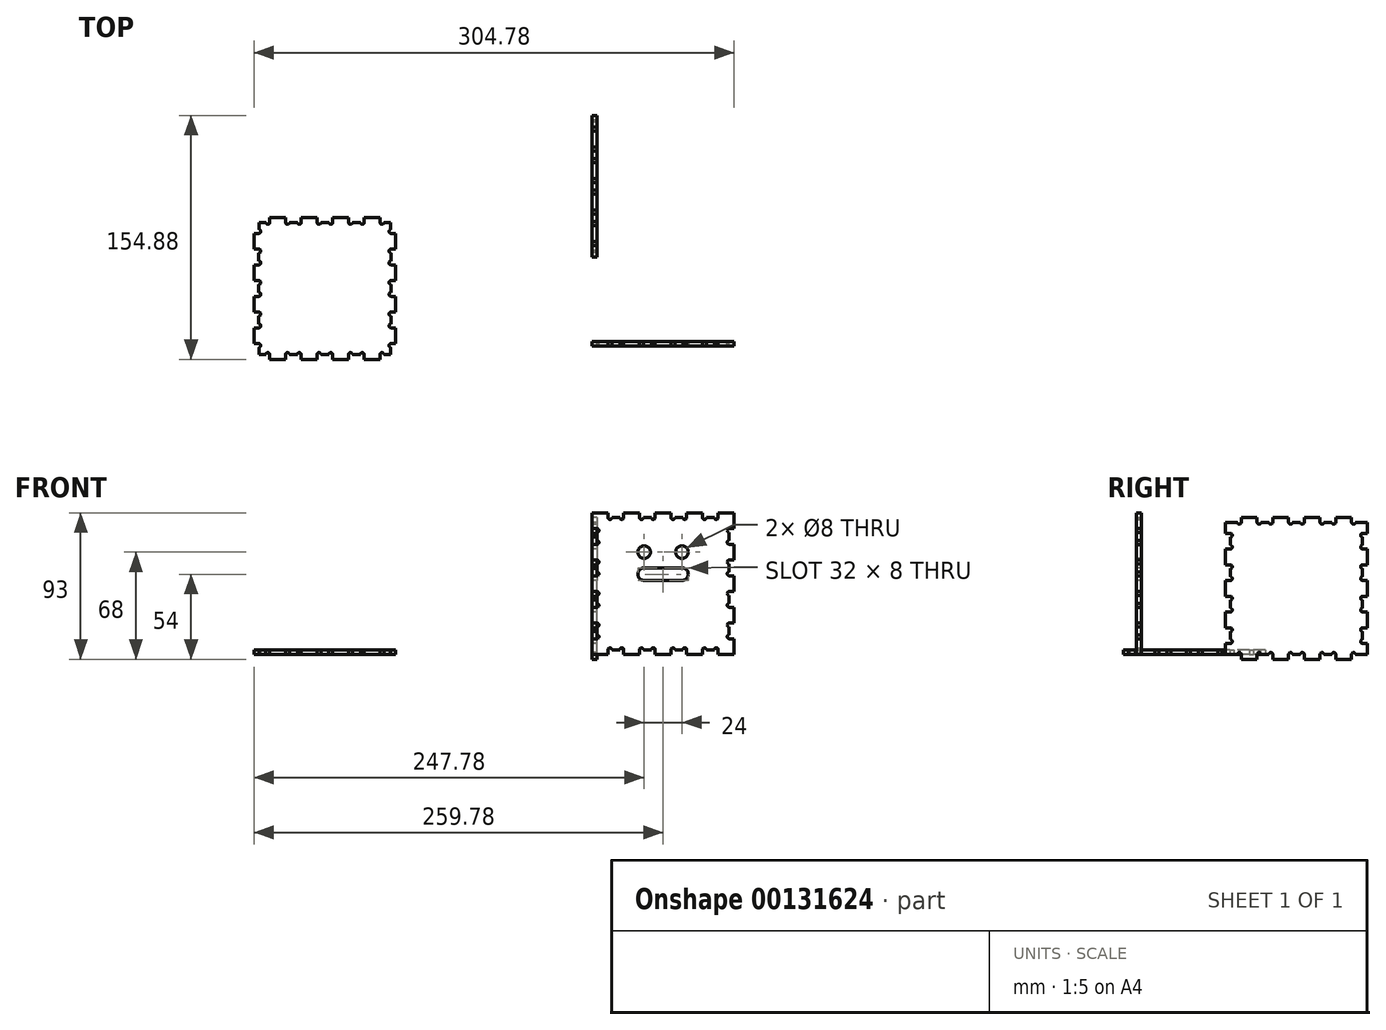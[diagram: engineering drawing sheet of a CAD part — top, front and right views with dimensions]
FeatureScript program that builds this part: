
annotation { "Feature Type Name" : "Feature", "Feature Type Description" : "" }
export const myFeature = defineFeature(function(context is Context, id is Id, definition is map)
    precondition{}
    {
        {
            var Q0;
            Q0=qCreatedBy(makeId("Front.planeOp"),FACE);
            var sketch = newSketch(context, id + "F0", { "sketchPlane" : qUnion([Q0])});
            skLineSegment(sketch, "E0.top", {"start": v(0, 90) * mm, "end": v(10, 90) * mm});
            skLineSegment(sketch, "E0.left", {"start": v(0, 0) * mm, "end": v(0, 10) * mm});
            skLineSegment(sketch, "E1.top", {"start": v(12.5, 87) * mm, "end": v(17.5, 87) * mm});
            skLineSegment(sketch, "E1.left", {"start": v(10, 90) * mm, "end": v(10, 87) * mm});
            skLineSegment(sketch, "E1.right", {"start": v(20, 90) * mm, "end": v(20, 87) * mm});
            skArc(sketch, "E2", {"start": v(10, 87) * mm, "mid": v(11.25, 85.75) * mm, "end": v(12.5, 87) * mm});
            skArc(sketch, "E3", {"start": v(17.5, 87) * mm, "mid": v(18.75, 85.75) * mm, "end": v(20, 87) * mm});
            skLineSegment(sketch, "E4.trimOffspring", {"start": v(20, 90) * mm, "end": v(30, 90) * mm});
            skLineSegment(sketch, "E5.1.0.0", {"start": v(32.5, 87) * mm, "end": v(37.5, 87) * mm});
            skLineSegment(sketch, "E5.1.0.1", {"start": v(30, 90) * mm, "end": v(30, 87) * mm});
            skLineSegment(sketch, "E5.1.0.2", {"start": v(40, 90) * mm, "end": v(40, 87) * mm});
            skArc(sketch, "E5.1.0.3", {"start": v(37.5, 87) * mm, "mid": v(38.75, 85.75) * mm, "end": v(40, 87) * mm});
            skArc(sketch, "E5.1.0.4", {"start": v(30, 87) * mm, "mid": v(31.25, 85.75) * mm, "end": v(32.5, 87) * mm});
            skLineSegment(sketch, "E5.2.0.0", {"start": v(52.5, 87) * mm, "end": v(57.5, 87) * mm});
            skLineSegment(sketch, "E5.2.0.1", {"start": v(50, 90) * mm, "end": v(50, 87) * mm});
            skLineSegment(sketch, "E5.2.0.2", {"start": v(60, 90) * mm, "end": v(60, 87) * mm});
            skArc(sketch, "E5.2.0.3", {"start": v(57.5, 87) * mm, "mid": v(58.75, 85.75) * mm, "end": v(60, 87) * mm});
            skArc(sketch, "E5.2.0.4", {"start": v(50, 87) * mm, "mid": v(51.25, 85.75) * mm, "end": v(52.5, 87) * mm});
            skLineSegment(sketch, "E5.3.0.0", {"start": v(72.5, 87) * mm, "end": v(77.5, 87) * mm});
            skLineSegment(sketch, "E5.3.0.1", {"start": v(70, 90) * mm, "end": v(70, 87) * mm});
            skLineSegment(sketch, "E5.3.0.2", {"start": v(80, 90) * mm, "end": v(80, 87) * mm});
            skArc(sketch, "E5.3.0.3", {"start": v(77.5, 87) * mm, "mid": v(78.75, 85.75) * mm, "end": v(80, 87) * mm});
            skArc(sketch, "E5.3.0.4", {"start": v(70, 87) * mm, "mid": v(71.25, 85.75) * mm, "end": v(72.5, 87) * mm});
            skLineSegment(sketch, "E5.direction1", {"start": v(10, 87) * mm, "end": v(30, 87) * mm, "construction": true});
            skLineSegment(sketch, "E6.trimOffspring", {"start": v(40, 90) * mm, "end": v(50, 90) * mm});
            skLineSegment(sketch, "E7.trimOffspring", {"start": v(60, 90) * mm, "end": v(70, 90) * mm});
            skLineSegment(sketch, "E8", {"start": v(0, 45) * mm, "end": v(0, 45) * mm});
            skLineSegment(sketch, "E9.MirrorCS", {"start": v(10, 3) * mm, "end": v(30, 3) * mm, "construction": true});
            skLineSegment(sketch, "E10.MirrorCS", {"start": v(12.5, 3) * mm, "end": v(17.5, 3) * mm});
            skArc(sketch, "E11.MirrorCS", {"start": v(17.5, 3) * mm, "mid": v(18.75, 4.25) * mm, "end": v(20, 3) * mm});
            skLineSegment(sketch, "E12.MirrorCS", {"start": v(60, 0) * mm, "end": v(70, 0) * mm});
            skLineSegment(sketch, "E13.MirrorCS", {"start": v(72.5, 3) * mm, "end": v(77.5, 3) * mm});
            skArc(sketch, "E14.MirrorCS", {"start": v(30, 3) * mm, "mid": v(31.25, 4.25) * mm, "end": v(32.5, 3) * mm});
            skLineSegment(sketch, "E15.MirrorCS", {"start": v(52.5, 3) * mm, "end": v(57.5, 3) * mm});
            skLineSegment(sketch, "E16.MirrorCS", {"start": v(50, 0) * mm, "end": v(50, 3) * mm});
            skLineSegment(sketch, "E17.MirrorCS", {"start": v(0, 0) * mm, "end": v(10, 0) * mm});
            skLineSegment(sketch, "E18.MirrorCS", {"start": v(10, 0) * mm, "end": v(10, 3) * mm});
            skLineSegment(sketch, "E19.MirrorCS", {"start": v(20, 0) * mm, "end": v(20, 3) * mm});
            skArc(sketch, "E20.MirrorCS", {"start": v(10, 3) * mm, "mid": v(11.25, 4.25) * mm, "end": v(12.5, 3) * mm});
            skLineSegment(sketch, "E21.MirrorCS", {"start": v(20, 0) * mm, "end": v(30, 0) * mm});
            skLineSegment(sketch, "E22.MirrorCS", {"start": v(32.5, 3) * mm, "end": v(37.5, 3) * mm});
            skLineSegment(sketch, "E23.MirrorCS", {"start": v(30, 0) * mm, "end": v(30, 3) * mm});
            skLineSegment(sketch, "E24.MirrorCS", {"start": v(40, 0) * mm, "end": v(40, 3) * mm});
            skArc(sketch, "E25.MirrorCS", {"start": v(37.5, 3) * mm, "mid": v(38.75, 4.25) * mm, "end": v(40, 3) * mm});
            skLineSegment(sketch, "E26.MirrorCS", {"start": v(80, 0) * mm, "end": v(90, 0) * mm});
            skArc(sketch, "E27.MirrorCS", {"start": v(70, 3) * mm, "mid": v(71.25, 4.25) * mm, "end": v(72.5, 3) * mm});
            skLineSegment(sketch, "E28.MirrorCS", {"start": v(70, 0) * mm, "end": v(70, 3) * mm});
            skArc(sketch, "E29.MirrorCS", {"start": v(57.5, 3) * mm, "mid": v(58.75, 4.25) * mm, "end": v(60, 3) * mm});
            skLineSegment(sketch, "E30.MirrorCS", {"start": v(80, 0) * mm, "end": v(80, 3) * mm});
            skArc(sketch, "E31.MirrorCS", {"start": v(50, 3) * mm, "mid": v(51.25, 4.25) * mm, "end": v(52.5, 3) * mm});
            skLineSegment(sketch, "E32.MirrorCS", {"start": v(40, 0) * mm, "end": v(50, 0) * mm});
            skLineSegment(sketch, "E33.MirrorCS", {"start": v(60, 0) * mm, "end": v(60, 3) * mm});
            skArc(sketch, "E34.MirrorCS", {"start": v(77.5, 3) * mm, "mid": v(78.75, 4.25) * mm, "end": v(80, 3) * mm});
            skLineSegment(sketch, "E35.bottom", {"start": v(0, 80) * mm, "end": v(3, 80) * mm});
            skLineSegment(sketch, "E35.top", {"start": v(0, 70) * mm, "end": v(3, 70) * mm});
            skLineSegment(sketch, "E35.right", {"start": v(3, 77.5) * mm, "end": v(3, 72.5) * mm});
            skArc(sketch, "E36", {"start": v(3, 77.5) * mm, "mid": v(4.25, 78.75) * mm, "end": v(3, 80) * mm});
            skArc(sketch, "E37", {"start": v(3, 70) * mm, "mid": v(4.25, 71.25) * mm, "end": v(3, 72.5) * mm});
            skLineSegment(sketch, "E38.trimOffspring", {"start": v(0, 80) * mm, "end": v(0, 90) * mm});
            skLineSegment(sketch, "E39.0.1.0", {"start": v(3, 57.5) * mm, "end": v(3, 52.5) * mm});
            skLineSegment(sketch, "E39.0.1.1", {"start": v(0, 50) * mm, "end": v(3, 50) * mm});
            skArc(sketch, "E39.0.1.2", {"start": v(3, 50) * mm, "mid": v(4.25, 51.25) * mm, "end": v(3, 52.5) * mm});
            skLineSegment(sketch, "E39.0.1.3", {"start": v(0, 60) * mm, "end": v(3, 60) * mm});
            skArc(sketch, "E39.0.1.4", {"start": v(3, 57.5) * mm, "mid": v(4.25, 58.75) * mm, "end": v(3, 60) * mm});
            skLineSegment(sketch, "E39.0.2.0", {"start": v(3, 37.5) * mm, "end": v(3, 32.5) * mm});
            skLineSegment(sketch, "E39.0.2.1", {"start": v(0, 30) * mm, "end": v(3, 30) * mm});
            skArc(sketch, "E39.0.2.2", {"start": v(3, 30) * mm, "mid": v(4.25, 31.25) * mm, "end": v(3, 32.5) * mm});
            skLineSegment(sketch, "E39.0.2.3", {"start": v(0, 40) * mm, "end": v(3, 40) * mm});
            skArc(sketch, "E39.0.2.4", {"start": v(3, 37.5) * mm, "mid": v(4.25, 38.75) * mm, "end": v(3, 40) * mm});
            skLineSegment(sketch, "E39.0.3.0", {"start": v(3, 17.5) * mm, "end": v(3, 12.5) * mm});
            skLineSegment(sketch, "E39.0.3.1", {"start": v(0, 10) * mm, "end": v(3, 10) * mm});
            skArc(sketch, "E39.0.3.2", {"start": v(3, 10) * mm, "mid": v(4.25, 11.25) * mm, "end": v(3, 12.5) * mm});
            skLineSegment(sketch, "E39.0.3.3", {"start": v(0, 20) * mm, "end": v(3, 20) * mm});
            skArc(sketch, "E39.0.3.4", {"start": v(3, 17.5) * mm, "mid": v(4.25, 18.75) * mm, "end": v(3, 20) * mm});
            skLineSegment(sketch, "E39.direction1", {"start": v(0, 70) * mm, "end": v(31.85, 70) * mm, "construction": true});
            skLineSegment(sketch, "E39.direction2", {"start": v(0, 70) * mm, "end": v(0, 60) * mm, "construction": true});
            skLineSegment(sketch, "E40.trimOffspring", {"start": v(0, 40) * mm, "end": v(0, 50) * mm});
            skLineSegment(sketch, "E41.trimOffspring", {"start": v(0, 60) * mm, "end": v(0, 70) * mm});
            skLineSegment(sketch, "E42.trimOffspring", {"start": v(0, 20) * mm, "end": v(0, 30) * mm});
            skPoint(sketch, "E0.right.start.orphan", {"position": v(90, 0) * mm});
            skLineSegment(sketch, "E43", {"start": v(45, 0) * mm, "end": v(45, 90) * mm, "construction": true});
            skLineSegment(sketch, "E44.MirrorCS", {"start": v(90, 60) * mm, "end": v(90, 70) * mm});
            skLineSegment(sketch, "E45.MirrorCS", {"start": v(87, 57.5) * mm, "end": v(87, 52.5) * mm});
            skLineSegment(sketch, "E46.MirrorCS", {"start": v(90, 70) * mm, "end": v(90, 60) * mm, "construction": true});
            skArc(sketch, "E47.MirrorCS", {"start": v(87, 50) * mm, "mid": v(85.75, 51.25) * mm, "end": v(87, 52.5) * mm});
            skArc(sketch, "E48.MirrorCS", {"start": v(87, 37.5) * mm, "mid": v(85.75, 38.75) * mm, "end": v(87, 40) * mm});
            skArc(sketch, "E49.MirrorCS", {"start": v(87, 70) * mm, "mid": v(85.75, 71.25) * mm, "end": v(87, 72.5) * mm});
            skArc(sketch, "E50.MirrorCS", {"start": v(87, 17.5) * mm, "mid": v(85.75, 18.75) * mm, "end": v(87, 20) * mm});
            skArc(sketch, "E51.MirrorCS", {"start": v(87, 30) * mm, "mid": v(85.75, 31.25) * mm, "end": v(87, 32.5) * mm});
            skLineSegment(sketch, "E52.MirrorCS", {"start": v(90, 20) * mm, "end": v(90, 30) * mm});
            skLineSegment(sketch, "E53.MirrorCS", {"start": v(90, 60) * mm, "end": v(87, 60) * mm});
            skLineSegment(sketch, "E54.MirrorCS", {"start": v(87, 17.5) * mm, "end": v(87, 12.5) * mm});
            skLineSegment(sketch, "E55.MirrorCS", {"start": v(90, 80) * mm, "end": v(87, 80) * mm});
            skArc(sketch, "E56.MirrorCS", {"start": v(87, 77.5) * mm, "mid": v(85.75, 78.75) * mm, "end": v(87, 80) * mm});
            skLineSegment(sketch, "E57.MirrorCS", {"start": v(87, 77.5) * mm, "end": v(87, 72.5) * mm});
            skLineSegment(sketch, "E58.MirrorCS", {"start": v(90, 10) * mm, "end": v(87, 10) * mm});
            skLineSegment(sketch, "E59.MirrorCS", {"start": v(90, 70) * mm, "end": v(87, 70) * mm});
            skArc(sketch, "E60.MirrorCS", {"start": v(87, 10) * mm, "mid": v(85.75, 11.25) * mm, "end": v(87, 12.5) * mm});
            skLineSegment(sketch, "E61.MirrorCS", {"start": v(90, 40) * mm, "end": v(87, 40) * mm});
            skLineSegment(sketch, "E62.MirrorCS", {"start": v(90, 50) * mm, "end": v(87, 50) * mm});
            skLineSegment(sketch, "E63.MirrorCS", {"start": v(87, 37.5) * mm, "end": v(87, 32.5) * mm});
            skLineSegment(sketch, "E64.MirrorCS", {"start": v(90, 20) * mm, "end": v(87, 20) * mm});
            skArc(sketch, "E65.MirrorCS", {"start": v(87, 57.5) * mm, "mid": v(85.75, 58.75) * mm, "end": v(87, 60) * mm});
            skLineSegment(sketch, "E66.MirrorCS", {"start": v(90, 30) * mm, "end": v(87, 30) * mm});
            skLineSegment(sketch, "E67.MirrorCS", {"start": v(90, 40) * mm, "end": v(90, 50) * mm});
            skLineSegment(sketch, "E68.MirrorCS", {"start": v(90, 0) * mm, "end": v(90, 10) * mm});
            skLineSegment(sketch, "E69.MirrorCS", {"start": v(90, 80) * mm, "end": v(90, 90) * mm});
            skLineSegment(sketch, "E70", {"start": v(80, 90) * mm, "end": v(90, 90) * mm});
            skLineSegment(sketch, "E71", {"start": v(90, 0) * mm, "end": v(80, 0) * mm});
            skLineSegment(sketch, "E72.trimOffspring", {"start": v(50, 90) * mm, "end": v(40, 90) * mm});
            skSolve(sketch);
        }
        {
            var Q0;
            Q0 = qSketchRegion(id + "F0", true);
            extrude(context, id + "F1", {"entities" : qUnion([Q0]), "depth" : 3 * mm});
        }
        {
            var Q0;
            Q0=qCreatedBy(makeId("Right.planeOp"),FACE);
            var sketch = newSketch(context, id + "F2", { "sketchPlane" : qUnion([Q0])});
            skLineSegment(sketch, "E73", {"start": v(53.51, 0) * mm, "end": v(53.51, 7) * mm});
            skLineSegment(sketch, "E74", {"start": v(53.51, 0) * mm, "end": v(61.01, 0) * mm});
            skLineSegment(sketch, "E75", {"start": v(63.51, -3) * mm, "end": v(63.51, 0) * mm});
            skLineSegment(sketch, "E76", {"start": v(63.51, -3) * mm, "end": v(73.51, -3) * mm});
            skLineSegment(sketch, "E77", {"start": v(73.51, 0) * mm, "end": v(73.51, -3) * mm});
            skLineSegment(sketch, "E78", {"start": v(83.51, -3) * mm, "end": v(83.51, 0) * mm});
            skLineSegment(sketch, "E79", {"start": v(83.51, -3) * mm, "end": v(93.51, -3) * mm});
            skLineSegment(sketch, "E80", {"start": v(93.51, -3) * mm, "end": v(93.51, 0) * mm});
            skLineSegment(sketch, "E81", {"start": v(96.01, 0) * mm, "end": v(98.51, 0) * mm});
            skArc(sketch, "E82", {"start": v(63.51, 0) * mm, "mid": v(62.26, 1.25) * mm, "end": v(61.01, 0) * mm});
            skArc(sketch, "E83", {"start": v(76.01, 0) * mm, "mid": v(74.76, 1.25) * mm, "end": v(73.51, 0) * mm});
            skArc(sketch, "E84", {"start": v(83.51, 0) * mm, "mid": v(82.26, 1.25) * mm, "end": v(81.01, 0) * mm});
            skArc(sketch, "E85", {"start": v(96.01, 0) * mm, "mid": v(94.76, 1.25) * mm, "end": v(93.51, 0) * mm});
            skLineSegment(sketch, "E86", {"start": v(76.01, 0) * mm, "end": v(81.01, 0) * mm});
            skLineSegment(sketch, "E87", {"start": v(98.51, 0) * mm, "end": v(98.51, 42.39) * mm, "construction": true});
            skLineSegment(sketch, "E88", {"start": v(53.51, 7) * mm, "end": v(56.51, 7) * mm});
            skLineSegment(sketch, "E89", {"start": v(56.51, 17) * mm, "end": v(53.51, 17) * mm});
            skLineSegment(sketch, "E90", {"start": v(53.51, 17) * mm, "end": v(53.51, 27) * mm});
            skLineSegment(sketch, "E91", {"start": v(53.51, 27) * mm, "end": v(56.51, 27) * mm});
            skLineSegment(sketch, "E92", {"start": v(56.51, 37) * mm, "end": v(53.51, 37) * mm});
            skArc(sketch, "E93", {"start": v(56.51, 7) * mm, "mid": v(57.76, 8.25) * mm, "end": v(56.51, 9.5) * mm});
            skArc(sketch, "E94", {"start": v(56.51, 14.5) * mm, "mid": v(57.76, 15.75) * mm, "end": v(56.51, 17) * mm});
            skArc(sketch, "E95", {"start": v(56.51, 27) * mm, "mid": v(57.76, 28.25) * mm, "end": v(56.51, 29.5) * mm});
            skArc(sketch, "E96", {"start": v(56.51, 34.5) * mm, "mid": v(57.76, 35.75) * mm, "end": v(56.51, 37) * mm});
            skLineSegment(sketch, "E97", {"start": v(53.51, 37) * mm, "end": v(53.51, 42) * mm});
            skLineSegment(sketch, "E98.trimOffspring", {"start": v(56.51, 29.5) * mm, "end": v(56.51, 34.5) * mm});
            skLineSegment(sketch, "E99", {"start": v(56.51, 14.5) * mm, "end": v(56.51, 9.5) * mm});
            skLineSegment(sketch, "E100", {"start": v(53.51, 42) * mm, "end": v(98.51, 42) * mm, "construction": true});
            skLineSegment(sketch, "E101.MirrorCS", {"start": v(143.51, 0) * mm, "end": v(136.01, 0) * mm});
            skArc(sketch, "E102.MirrorCS", {"start": v(113.51, 0) * mm, "mid": v(114.76, 1.25) * mm, "end": v(116.01, 0) * mm});
            skLineSegment(sketch, "E103.MirrorCS", {"start": v(103.51, -3) * mm, "end": v(103.51, 0) * mm});
            skLineSegment(sketch, "E104.MirrorCS", {"start": v(113.51, -3) * mm, "end": v(113.51, 0) * mm});
            skLineSegment(sketch, "E105.MirrorCS", {"start": v(121.01, 0) * mm, "end": v(116.01, 0) * mm});
            skLineSegment(sketch, "E106.MirrorCS", {"start": v(143.51, 0) * mm, "end": v(143.51, 7) * mm});
            skArc(sketch, "E107.MirrorCS", {"start": v(133.51, 0) * mm, "mid": v(134.76, 1.25) * mm, "end": v(136.01, 0) * mm});
            skLineSegment(sketch, "E108.MirrorCS", {"start": v(113.51, -3) * mm, "end": v(103.51, -3) * mm});
            skLineSegment(sketch, "E109.MirrorCS", {"start": v(101.01, 0) * mm, "end": v(98.51, 0) * mm});
            skArc(sketch, "E110.MirrorCS", {"start": v(101.01, 0) * mm, "mid": v(102.26, 1.25) * mm, "end": v(103.51, 0) * mm});
            skLineSegment(sketch, "E111.MirrorCS", {"start": v(133.51, -3) * mm, "end": v(133.51, 0) * mm});
            skLineSegment(sketch, "E112.MirrorCS", {"start": v(133.51, -3) * mm, "end": v(123.51, -3) * mm});
            skLineSegment(sketch, "E113.MirrorCS", {"start": v(123.51, 0) * mm, "end": v(123.51, -3) * mm});
            skArc(sketch, "E114.MirrorCS", {"start": v(121.01, 0) * mm, "mid": v(122.26, 1.25) * mm, "end": v(123.51, 0) * mm});
            skArc(sketch, "E115.MirrorCS", {"start": v(140.51, 14.5) * mm, "mid": v(139.26, 15.75) * mm, "end": v(140.51, 17) * mm});
            skLineSegment(sketch, "E116.MirrorCS", {"start": v(140.51, 37) * mm, "end": v(143.51, 37) * mm});
            skLineSegment(sketch, "E117.MirrorCS", {"start": v(143.51, 27) * mm, "end": v(140.51, 27) * mm});
            skArc(sketch, "E118.MirrorCS", {"start": v(140.51, 27) * mm, "mid": v(139.26, 28.25) * mm, "end": v(140.51, 29.5) * mm});
            skLineSegment(sketch, "E119.MirrorCS", {"start": v(140.51, 29.5) * mm, "end": v(140.51, 34.5) * mm});
            skLineSegment(sketch, "E120.MirrorCS", {"start": v(140.51, 14.5) * mm, "end": v(140.51, 9.5) * mm});
            skLineSegment(sketch, "E121.MirrorCS", {"start": v(140.51, 17) * mm, "end": v(143.51, 17) * mm});
            skLineSegment(sketch, "E122.MirrorCS", {"start": v(143.51, 17) * mm, "end": v(143.51, 27) * mm});
            skArc(sketch, "E123.MirrorCS", {"start": v(140.51, 7) * mm, "mid": v(139.26, 8.25) * mm, "end": v(140.51, 9.5) * mm});
            skArc(sketch, "E124.MirrorCS", {"start": v(140.51, 34.5) * mm, "mid": v(139.26, 35.75) * mm, "end": v(140.51, 37) * mm});
            skLineSegment(sketch, "E125.MirrorCS", {"start": v(143.51, 7) * mm, "end": v(140.51, 7) * mm});
            skLineSegment(sketch, "E126.MirrorCS", {"start": v(143.51, 37) * mm, "end": v(143.51, 42) * mm});
            skLineSegment(sketch, "E127.MirrorCS", {"start": v(56.51, 69.5) * mm, "end": v(56.51, 74.5) * mm});
            skLineSegment(sketch, "E128.MirrorCS", {"start": v(103.51, 87) * mm, "end": v(103.51, 84) * mm});
            skArc(sketch, "E129.MirrorCS", {"start": v(56.51, 57) * mm, "mid": v(57.76, 55.75) * mm, "end": v(56.51, 54.5) * mm});
            skLineSegment(sketch, "E130.MirrorCS", {"start": v(140.51, 69.5) * mm, "end": v(140.51, 74.5) * mm});
            skArc(sketch, "E131.MirrorCS", {"start": v(133.51, 84) * mm, "mid": v(134.76, 82.75) * mm, "end": v(136.01, 84) * mm});
            skLineSegment(sketch, "E132.MirrorCS", {"start": v(56.51, 54.5) * mm, "end": v(56.51, 49.5) * mm});
            skLineSegment(sketch, "E133.MirrorCS", {"start": v(133.51, 87) * mm, "end": v(123.51, 87) * mm});
            skLineSegment(sketch, "E134.MirrorCS", {"start": v(143.51, 57) * mm, "end": v(140.51, 57) * mm});
            skLineSegment(sketch, "E135.MirrorCS", {"start": v(113.51, 87) * mm, "end": v(103.51, 87) * mm});
            skLineSegment(sketch, "E136.MirrorCS", {"start": v(53.51, 57) * mm, "end": v(56.51, 57) * mm});
            skArc(sketch, "E137.MirrorCS", {"start": v(96.01, 84) * mm, "mid": v(94.76, 82.75) * mm, "end": v(93.51, 84) * mm});
            skArc(sketch, "E138.MirrorCS", {"start": v(101.01, 84) * mm, "mid": v(102.26, 82.75) * mm, "end": v(103.51, 84) * mm});
            skArc(sketch, "E139.MirrorCS", {"start": v(56.51, 77) * mm, "mid": v(57.76, 75.75) * mm, "end": v(56.51, 74.5) * mm});
            skLineSegment(sketch, "E140.MirrorCS", {"start": v(143.51, 77) * mm, "end": v(140.51, 77) * mm});
            skLineSegment(sketch, "E141.MirrorCS", {"start": v(56.51, 47) * mm, "end": v(53.51, 47) * mm});
            skLineSegment(sketch, "E142.MirrorCS", {"start": v(53.51, 84) * mm, "end": v(53.51, 77) * mm});
            skArc(sketch, "E143.MirrorCS", {"start": v(121.01, 84) * mm, "mid": v(122.26, 82.75) * mm, "end": v(123.51, 84) * mm});
            skLineSegment(sketch, "E144.MirrorCS", {"start": v(76.01, 84) * mm, "end": v(81.01, 84) * mm});
            skLineSegment(sketch, "E145.MirrorCS", {"start": v(140.51, 67) * mm, "end": v(143.51, 67) * mm});
            skLineSegment(sketch, "E146.MirrorCS", {"start": v(140.51, 47) * mm, "end": v(143.51, 47) * mm});
            skLineSegment(sketch, "E147.MirrorCS", {"start": v(143.51, 67) * mm, "end": v(143.51, 57) * mm});
            skArc(sketch, "E148.MirrorCS", {"start": v(56.51, 49.5) * mm, "mid": v(57.76, 48.25) * mm, "end": v(56.51, 47) * mm});
            skLineSegment(sketch, "E149.MirrorCS", {"start": v(113.51, 87) * mm, "end": v(113.51, 84) * mm});
            skLineSegment(sketch, "E150.MirrorCS", {"start": v(143.51, 84) * mm, "end": v(136.01, 84) * mm});
            skLineSegment(sketch, "E151.MirrorCS", {"start": v(140.51, 54.5) * mm, "end": v(140.51, 49.5) * mm});
            skLineSegment(sketch, "E152.MirrorCS", {"start": v(143.51, 84) * mm, "end": v(143.51, 77) * mm});
            skLineSegment(sketch, "E153.MirrorCS", {"start": v(53.51, 77) * mm, "end": v(56.51, 77) * mm});
            skArc(sketch, "E154.MirrorCS", {"start": v(140.51, 69.5) * mm, "mid": v(139.26, 68.25) * mm, "end": v(140.51, 67) * mm});
            skArc(sketch, "E155.MirrorCS", {"start": v(113.51, 84) * mm, "mid": v(114.76, 82.75) * mm, "end": v(116.01, 84) * mm});
            skArc(sketch, "E156.MirrorCS", {"start": v(140.51, 49.5) * mm, "mid": v(139.26, 48.25) * mm, "end": v(140.51, 47) * mm});
            skLineSegment(sketch, "E157.MirrorCS", {"start": v(133.51, 87) * mm, "end": v(133.51, 84) * mm});
            skLineSegment(sketch, "E158.MirrorCS", {"start": v(53.51, 67) * mm, "end": v(53.51, 57) * mm});
            skLineSegment(sketch, "E159.MirrorCS", {"start": v(53.51, 47) * mm, "end": v(53.51, 42) * mm});
            skArc(sketch, "E160.MirrorCS", {"start": v(140.51, 77) * mm, "mid": v(139.26, 75.75) * mm, "end": v(140.51, 74.5) * mm});
            skLineSegment(sketch, "E161.MirrorCS", {"start": v(101.01, 84) * mm, "end": v(98.51, 84) * mm});
            skArc(sketch, "E162.MirrorCS", {"start": v(140.51, 57) * mm, "mid": v(139.26, 55.75) * mm, "end": v(140.51, 54.5) * mm});
            skLineSegment(sketch, "E163.MirrorCS", {"start": v(121.01, 84) * mm, "end": v(116.01, 84) * mm});
            skLineSegment(sketch, "E164.MirrorCS", {"start": v(56.51, 67) * mm, "end": v(53.51, 67) * mm});
            skLineSegment(sketch, "E165.MirrorCS", {"start": v(98.51, 84) * mm, "end": v(98.51, 41.61) * mm, "construction": true});
            skArc(sketch, "E166.MirrorCS", {"start": v(83.51, 84) * mm, "mid": v(82.26, 82.75) * mm, "end": v(81.01, 84) * mm});
            skArc(sketch, "E167.MirrorCS", {"start": v(76.01, 84) * mm, "mid": v(74.76, 82.75) * mm, "end": v(73.51, 84) * mm});
            skArc(sketch, "E168.MirrorCS", {"start": v(63.51, 84) * mm, "mid": v(62.26, 82.75) * mm, "end": v(61.01, 84) * mm});
            skLineSegment(sketch, "E169.MirrorCS", {"start": v(96.01, 84) * mm, "end": v(98.51, 84) * mm});
            skLineSegment(sketch, "E170.MirrorCS", {"start": v(93.51, 87) * mm, "end": v(93.51, 84) * mm});
            skLineSegment(sketch, "E171.MirrorCS", {"start": v(83.51, 87) * mm, "end": v(93.51, 87) * mm});
            skLineSegment(sketch, "E172.MirrorCS", {"start": v(83.51, 87) * mm, "end": v(83.51, 84) * mm});
            skLineSegment(sketch, "E173.MirrorCS", {"start": v(73.51, 84) * mm, "end": v(73.51, 87) * mm});
            skLineSegment(sketch, "E174.MirrorCS", {"start": v(63.51, 87) * mm, "end": v(73.51, 87) * mm});
            skArc(sketch, "E175.MirrorCS", {"start": v(56.51, 69.5) * mm, "mid": v(57.76, 68.25) * mm, "end": v(56.51, 67) * mm});
            skLineSegment(sketch, "E176.MirrorCS", {"start": v(63.51, 87) * mm, "end": v(63.51, 84) * mm});
            skLineSegment(sketch, "E177.MirrorCS", {"start": v(53.51, 84) * mm, "end": v(61.01, 84) * mm});
            skLineSegment(sketch, "E178.MirrorCS", {"start": v(123.51, 84) * mm, "end": v(123.51, 87) * mm});
            skLineSegment(sketch, "E179.MirrorCS", {"start": v(143.51, 47) * mm, "end": v(143.51, 42) * mm});
            skSolve(sketch);
        }
        {
            var Q0;
            Q0=makeQuery(id+"F2.imprint","IMPRINT",FACE,{"disambiguationData":[TD([[makeQuery(id+"F2.imprint","IMPRINT",EDGE,{"derivedFrom":sQuery(id+"F2.wireOp",EDGE,"E73")}),-1.0]])]});
            extrude(context, id + "F3", {"entities" : qUnion([Q0]), "depth" : 3 * mm});
        }
        {
            var Q0;
            Q0=qCreatedBy(makeId("Top.planeOp"),FACE);
            var sketch = newSketch(context, id + "F4", { "sketchPlane" : qUnion([Q0])});
            skLineSegment(sketch, "E180", {"start": v(-211.57, -8.37) * mm, "end": v(-211.57, -3.85) * mm});
            skLineSegment(sketch, "E181", {"start": v(-211.78, -1.37) * mm, "end": v(-214.78, -1.37) * mm});
            skLineSegment(sketch, "E182", {"start": v(-214.78, -1.37) * mm, "end": v(-214.78, 8.63) * mm});
            skLineSegment(sketch, "E183", {"start": v(-214.78, 8.63) * mm, "end": v(-211.78, 8.63) * mm});
            skLineSegment(sketch, "E184", {"start": v(-211.78, 18.63) * mm, "end": v(-214.78, 18.63) * mm});
            skLineSegment(sketch, "E185", {"start": v(-214.78, 18.63) * mm, "end": v(-214.78, 28.63) * mm});
            skLineSegment(sketch, "E186", {"start": v(-214.78, 28.63) * mm, "end": v(-211.78, 28.63) * mm});
            skArc(sketch, "E187", {"start": v(-211.57, -3.85) * mm, "mid": v(-210.54, -2.51) * mm, "end": v(-211.78, -1.37) * mm});
            skArc(sketch, "E188", {"start": v(-211.78, 8.63) * mm, "mid": v(-210.53, 9.88) * mm, "end": v(-211.78, 11.13) * mm});
            skArc(sketch, "E189", {"start": v(-211.78, 16.13) * mm, "mid": v(-210.53, 17.38) * mm, "end": v(-211.78, 18.63) * mm});
            skArc(sketch, "E190", {"start": v(-211.78, 28.63) * mm, "mid": v(-210.53, 29.88) * mm, "end": v(-211.78, 31.13) * mm});
            skLineSegment(sketch, "E191", {"start": v(-211.78, 31.13) * mm, "end": v(-211.78, 33.63) * mm});
            skLineSegment(sketch, "E192.trimOffspring", {"start": v(-211.78, 11.13) * mm, "end": v(-211.78, 16.13) * mm});
            skLineSegment(sketch, "E193", {"start": v(-169.78, -8.37) * mm, "end": v(-169.78, 33.63) * mm, "construction": true});
            skArc(sketch, "E194.MirrorCS", {"start": v(-154.78, -8.37) * mm, "mid": v(-153.53, -7.12) * mm, "end": v(-152.28, -8.37) * mm});
            skLineSegment(sketch, "E195.MirrorCS", {"start": v(-167.28, -8.37) * mm, "end": v(-169.78, -8.37) * mm});
            skArc(sketch, "E196.MirrorCS", {"start": v(-147.28, -8.37) * mm, "mid": v(-146.03, -7.12) * mm, "end": v(-144.78, -8.37) * mm});
            skLineSegment(sketch, "E197.MirrorCS", {"start": v(-127.78, 31.13) * mm, "end": v(-127.78, 33.63) * mm});
            skLineSegment(sketch, "E198.MirrorCS", {"start": v(-154.78, -11.37) * mm, "end": v(-164.78, -11.37) * mm});
            skLineSegment(sketch, "E199.MirrorCS", {"start": v(-144.78, -8.37) * mm, "end": v(-144.78, -11.37) * mm});
            skLineSegment(sketch, "E200.MirrorCS", {"start": v(-164.78, -11.37) * mm, "end": v(-164.78, -8.37) * mm});
            skArc(sketch, "E201.MirrorCS", {"start": v(-134.78, -8.37) * mm, "mid": v(-133.53, -7.12) * mm, "end": v(-132.28, -8.37) * mm});
            skLineSegment(sketch, "E202.MirrorCS", {"start": v(-124.78, 28.63) * mm, "end": v(-127.78, 28.63) * mm});
            skLineSegment(sketch, "E203.MirrorCS", {"start": v(-124.78, 8.63) * mm, "end": v(-127.78, 8.63) * mm});
            skLineSegment(sketch, "E204.MirrorCS", {"start": v(-124.78, -1.37) * mm, "end": v(-124.78, 8.63) * mm});
            skArc(sketch, "E205.MirrorCS", {"start": v(-127.78, 28.63) * mm, "mid": v(-129.03, 29.88) * mm, "end": v(-127.78, 31.13) * mm});
            skArc(sketch, "E206.MirrorCS", {"start": v(-127.78, 16.13) * mm, "mid": v(-129.03, 17.38) * mm, "end": v(-127.78, 18.63) * mm});
            skLineSegment(sketch, "E207.MirrorCS", {"start": v(-127.78, -1.37) * mm, "end": v(-124.78, -1.37) * mm});
            skLineSegment(sketch, "E208.MirrorCS", {"start": v(-128, -8.37) * mm, "end": v(-128, -3.85) * mm});
            skLineSegment(sketch, "E209.MirrorCS", {"start": v(-134.78, -11.37) * mm, "end": v(-144.78, -11.37) * mm});
            skLineSegment(sketch, "E210.MirrorCS", {"start": v(-147.28, -8.37) * mm, "end": v(-152.28, -8.37) * mm});
            skLineSegment(sketch, "E211.MirrorCS", {"start": v(-127.78, 11.13) * mm, "end": v(-127.78, 16.13) * mm});
            skLineSegment(sketch, "E212.MirrorCS", {"start": v(-134.78, -11.37) * mm, "end": v(-134.78, -8.37) * mm});
            skArc(sketch, "E213.MirrorCS", {"start": v(-167.28, -8.37) * mm, "mid": v(-166.03, -7.12) * mm, "end": v(-164.78, -8.37) * mm});
            skLineSegment(sketch, "E214.MirrorCS", {"start": v(-124.78, 18.63) * mm, "end": v(-124.78, 28.63) * mm});
            skArc(sketch, "E215.MirrorCS", {"start": v(-128, -3.85) * mm, "mid": v(-129.03, -2.51) * mm, "end": v(-127.78, -1.37) * mm});
            skLineSegment(sketch, "E216.MirrorCS", {"start": v(-127.78, 18.63) * mm, "end": v(-124.78, 18.63) * mm});
            skLineSegment(sketch, "E217.MirrorCS", {"start": v(-154.78, -11.37) * mm, "end": v(-154.78, -8.37) * mm});
            skLineSegment(sketch, "E218.MirrorCS", {"start": v(-128, -8.37) * mm, "end": v(-132.28, -8.37) * mm});
            skArc(sketch, "E219.MirrorCS", {"start": v(-127.78, 8.63) * mm, "mid": v(-129.03, 9.88) * mm, "end": v(-127.78, 11.13) * mm});
            skLineSegment(sketch, "E220", {"start": v(-127.78, 33.63) * mm, "end": v(-211.78, 33.63) * mm, "construction": true});
            skArc(sketch, "E221.MirrorCS", {"start": v(-128, 71.12) * mm, "mid": v(-129.03, 69.78) * mm, "end": v(-127.78, 68.63) * mm});
            skLineSegment(sketch, "E222.MirrorCS", {"start": v(-147.28, 75.63) * mm, "end": v(-152.28, 75.63) * mm});
            skArc(sketch, "E223.MirrorCS", {"start": v(-154.78, 75.63) * mm, "mid": v(-153.53, 74.38) * mm, "end": v(-152.28, 75.63) * mm});
            skArc(sketch, "E224.MirrorCS", {"start": v(-184.78, 75.63) * mm, "mid": v(-186.03, 74.38) * mm, "end": v(-187.28, 75.63) * mm});
            skArc(sketch, "E225.MirrorCS", {"start": v(-127.78, 51.13) * mm, "mid": v(-129.03, 49.88) * mm, "end": v(-127.78, 48.63) * mm});
            skArc(sketch, "E226.MirrorCS", {"start": v(-147.28, 75.63) * mm, "mid": v(-146.03, 74.38) * mm, "end": v(-144.78, 75.63) * mm});
            skLineSegment(sketch, "E227.MirrorCS", {"start": v(-124.78, 58.63) * mm, "end": v(-127.78, 58.63) * mm});
            skLineSegment(sketch, "E228.MirrorCS", {"start": v(-172.28, 75.63) * mm, "end": v(-169.78, 75.63) * mm});
            skArc(sketch, "E229.MirrorCS", {"start": v(-127.78, 58.63) * mm, "mid": v(-129.03, 57.38) * mm, "end": v(-127.78, 56.13) * mm});
            skLineSegment(sketch, "E230.MirrorCS", {"start": v(-134.78, 78.63) * mm, "end": v(-134.78, 75.63) * mm});
            skLineSegment(sketch, "E231.MirrorCS", {"start": v(-144.78, 75.63) * mm, "end": v(-144.78, 78.63) * mm});
            skLineSegment(sketch, "E232.MirrorCS", {"start": v(-194.78, 75.63) * mm, "end": v(-194.78, 78.63) * mm});
            skLineSegment(sketch, "E233.MirrorCS", {"start": v(-214.78, 58.63) * mm, "end": v(-211.78, 58.63) * mm});
            skLineSegment(sketch, "E234.MirrorCS", {"start": v(-128, 75.63) * mm, "end": v(-132.28, 75.63) * mm});
            skLineSegment(sketch, "E235.MirrorCS", {"start": v(-127.78, 68.63) * mm, "end": v(-124.78, 68.63) * mm});
            skLineSegment(sketch, "E236.MirrorCS", {"start": v(-211.78, 48.63) * mm, "end": v(-214.78, 48.63) * mm});
            skLineSegment(sketch, "E237.MirrorCS", {"start": v(-127.78, 36.13) * mm, "end": v(-127.78, 33.63) * mm});
            skLineSegment(sketch, "E238.MirrorCS", {"start": v(-174.78, 78.63) * mm, "end": v(-174.78, 75.63) * mm});
            skLineSegment(sketch, "E239.MirrorCS", {"start": v(-204.78, 78.63) * mm, "end": v(-204.78, 75.63) * mm});
            skLineSegment(sketch, "E240.MirrorCS", {"start": v(-124.78, 68.63) * mm, "end": v(-124.78, 58.63) * mm});
            skArc(sketch, "E241.MirrorCS", {"start": v(-204.78, 75.63) * mm, "mid": v(-206.03, 74.38) * mm, "end": v(-207.28, 75.63) * mm});
            skLineSegment(sketch, "E242.MirrorCS", {"start": v(-167.28, 75.63) * mm, "end": v(-169.78, 75.63) * mm});
            skLineSegment(sketch, "E243.MirrorCS", {"start": v(-211.57, 75.63) * mm, "end": v(-207.28, 75.63) * mm});
            skArc(sketch, "E244.MirrorCS", {"start": v(-167.28, 75.63) * mm, "mid": v(-166.03, 74.38) * mm, "end": v(-164.78, 75.63) * mm});
            skLineSegment(sketch, "E245.MirrorCS", {"start": v(-164.78, 78.63) * mm, "end": v(-164.78, 75.63) * mm});
            skLineSegment(sketch, "E246.MirrorCS", {"start": v(-184.78, 78.63) * mm, "end": v(-184.78, 75.63) * mm});
            skLineSegment(sketch, "E247.MirrorCS", {"start": v(-127.78, 48.63) * mm, "end": v(-124.78, 48.63) * mm});
            skLineSegment(sketch, "E248.MirrorCS", {"start": v(-127.78, 56.13) * mm, "end": v(-127.78, 51.13) * mm});
            skLineSegment(sketch, "E249.MirrorCS", {"start": v(-124.78, 48.63) * mm, "end": v(-124.78, 38.63) * mm});
            skLineSegment(sketch, "E250.MirrorCS", {"start": v(-154.78, 78.63) * mm, "end": v(-164.78, 78.63) * mm});
            skArc(sketch, "E251.MirrorCS", {"start": v(-127.78, 38.63) * mm, "mid": v(-129.03, 37.38) * mm, "end": v(-127.78, 36.13) * mm});
            skLineSegment(sketch, "E252.MirrorCS", {"start": v(-211.78, 68.63) * mm, "end": v(-214.78, 68.63) * mm});
            skLineSegment(sketch, "E253.MirrorCS", {"start": v(-211.78, 56.13) * mm, "end": v(-211.78, 51.13) * mm});
            skLineSegment(sketch, "E254.MirrorCS", {"start": v(-128, 75.63) * mm, "end": v(-128, 71.12) * mm});
            skLineSegment(sketch, "E255.MirrorCS", {"start": v(-192.28, 75.63) * mm, "end": v(-187.28, 75.63) * mm});
            skArc(sketch, "E256.MirrorCS", {"start": v(-192.28, 75.63) * mm, "mid": v(-193.53, 74.38) * mm, "end": v(-194.78, 75.63) * mm});
            skLineSegment(sketch, "E257.MirrorCS", {"start": v(-134.78, 78.63) * mm, "end": v(-144.78, 78.63) * mm});
            skLineSegment(sketch, "E258.MirrorCS", {"start": v(-211.78, 36.13) * mm, "end": v(-211.78, 33.63) * mm});
            skLineSegment(sketch, "E259.MirrorCS", {"start": v(-169.78, 75.63) * mm, "end": v(-169.78, 33.63) * mm, "construction": true});
            skLineSegment(sketch, "E260.MirrorCS", {"start": v(-214.78, 68.63) * mm, "end": v(-214.78, 58.63) * mm});
            skLineSegment(sketch, "E261.MirrorCS", {"start": v(-184.78, 78.63) * mm, "end": v(-174.78, 78.63) * mm});
            skArc(sketch, "E262.MirrorCS", {"start": v(-211.78, 38.63) * mm, "mid": v(-210.53, 37.38) * mm, "end": v(-211.78, 36.13) * mm});
            skArc(sketch, "E263.MirrorCS", {"start": v(-211.78, 58.63) * mm, "mid": v(-210.53, 57.38) * mm, "end": v(-211.78, 56.13) * mm});
            skLineSegment(sketch, "E264.MirrorCS", {"start": v(-204.78, 78.63) * mm, "end": v(-194.78, 78.63) * mm});
            skArc(sketch, "E265.MirrorCS", {"start": v(-211.57, 71.12) * mm, "mid": v(-210.54, 69.78) * mm, "end": v(-211.78, 68.63) * mm});
            skLineSegment(sketch, "E266.MirrorCS", {"start": v(-214.78, 38.63) * mm, "end": v(-211.78, 38.63) * mm});
            skLineSegment(sketch, "E267.MirrorCS", {"start": v(-211.57, 75.63) * mm, "end": v(-211.57, 71.12) * mm});
            skLineSegment(sketch, "E268.MirrorCS", {"start": v(-124.78, 38.63) * mm, "end": v(-127.78, 38.63) * mm});
            skLineSegment(sketch, "E269.MirrorCS", {"start": v(-214.78, 48.63) * mm, "end": v(-214.78, 38.63) * mm});
            skArc(sketch, "E270.MirrorCS", {"start": v(-172.28, 75.63) * mm, "mid": v(-173.53, 74.38) * mm, "end": v(-174.78, 75.63) * mm});
            skArc(sketch, "E271.MirrorCS", {"start": v(-134.78, 75.63) * mm, "mid": v(-133.53, 74.38) * mm, "end": v(-132.28, 75.63) * mm});
            skLineSegment(sketch, "E272.MirrorCS", {"start": v(-154.78, 78.63) * mm, "end": v(-154.78, 75.63) * mm});
            skArc(sketch, "E273.MirrorCS", {"start": v(-211.78, 51.13) * mm, "mid": v(-210.53, 49.88) * mm, "end": v(-211.78, 48.63) * mm});
            skLineSegment(sketch, "E274.MirrorCS", {"start": v(-211.57, -8.37) * mm, "end": v(-207.28, -8.37) * mm});
            skLineSegment(sketch, "E275.MirrorCS", {"start": v(-184.78, -11.37) * mm, "end": v(-184.78, -8.37) * mm});
            skLineSegment(sketch, "E276.MirrorCS", {"start": v(-172.28, -8.37) * mm, "end": v(-169.78, -8.37) * mm});
            skLineSegment(sketch, "E277.MirrorCS", {"start": v(-194.78, -8.37) * mm, "end": v(-194.78, -11.37) * mm});
            skLineSegment(sketch, "E278.MirrorCS", {"start": v(-204.78, -11.37) * mm, "end": v(-204.78, -8.37) * mm});
            skArc(sketch, "E279.MirrorCS", {"start": v(-192.28, -8.37) * mm, "mid": v(-193.53, -7.12) * mm, "end": v(-194.78, -8.37) * mm});
            skArc(sketch, "E280.MirrorCS", {"start": v(-204.78, -8.37) * mm, "mid": v(-206.03, -7.12) * mm, "end": v(-207.28, -8.37) * mm});
            skLineSegment(sketch, "E281.MirrorCS", {"start": v(-174.78, -11.37) * mm, "end": v(-174.78, -8.37) * mm});
            skArc(sketch, "E282.MirrorCS", {"start": v(-184.78, -8.37) * mm, "mid": v(-186.03, -7.12) * mm, "end": v(-187.28, -8.37) * mm});
            skLineSegment(sketch, "E283.MirrorCS", {"start": v(-184.78, -11.37) * mm, "end": v(-174.78, -11.37) * mm});
            skArc(sketch, "E284.MirrorCS", {"start": v(-172.28, -8.37) * mm, "mid": v(-173.53, -7.12) * mm, "end": v(-174.78, -8.37) * mm});
            skLineSegment(sketch, "E285.MirrorCS", {"start": v(-204.78, -11.37) * mm, "end": v(-194.78, -11.37) * mm});
            skLineSegment(sketch, "E286.MirrorCS", {"start": v(-192.28, -8.37) * mm, "end": v(-187.28, -8.37) * mm});
            skSolve(sketch);
        }
        {
            var Q0;
            Q0 = qSketchRegion(id + "F4", true);
            extrude(context, id + "F5", {"entities" : qUnion([Q0]), "depth" : 3 * mm});
        }
        {
            var Q0;
            Q0=makeQuery(id+"F1.opExtrude","CAP_FACE",FACE,{"disambiguationData":[OSD([sQuery(id+"F0.wireOp",EDGE,"E0.top"),sQuery(id+"F0.wireOp",EDGE,"E0.left"),sQuery(id+"F0.wireOp",EDGE,"E1.top"),sQuery(id+"F0.wireOp",EDGE,"E1.left"),sQuery(id+"F0.wireOp",EDGE,"E1.right"),sQuery(id+"F0.wireOp",EDGE,"E2"),sQuery(id+"F0.wireOp",EDGE,"E3"),sQuery(id+"F0.wireOp",EDGE,"E4.trimOffspring"),sQuery(id+"F0.wireOp",EDGE,"E5.1.0.0"),sQuery(id+"F0.wireOp",EDGE,"E5.1.0.1"),sQuery(id+"F0.wireOp",EDGE,"E5.1.0.2"),sQuery(id+"F0.wireOp",EDGE,"E5.1.0.3"),sQuery(id+"F0.wireOp",EDGE,"E5.1.0.4"),sQuery(id+"F0.wireOp",EDGE,"E5.2.0.0"),sQuery(id+"F0.wireOp",EDGE,"E5.2.0.1"),sQuery(id+"F0.wireOp",EDGE,"E5.2.0.2"),sQuery(id+"F0.wireOp",EDGE,"E5.2.0.3"),sQuery(id+"F0.wireOp",EDGE,"E5.2.0.4"),sQuery(id+"F0.wireOp",EDGE,"E5.3.0.0"),sQuery(id+"F0.wireOp",EDGE,"E5.3.0.1"),sQuery(id+"F0.wireOp",EDGE,"E5.3.0.2"),sQuery(id+"F0.wireOp",EDGE,"E5.3.0.3"),sQuery(id+"F0.wireOp",EDGE,"E5.3.0.4"),sQuery(id+"F0.wireOp",EDGE,"E7.trimOffspring"),sQuery(id+"F0.wireOp",EDGE,"E10.MirrorCS"),sQuery(id+"F0.wireOp",EDGE,"E11.MirrorCS"),sQuery(id+"F0.wireOp",EDGE,"E12.MirrorCS"),sQuery(id+"F0.wireOp",EDGE,"E13.MirrorCS"),sQuery(id+"F0.wireOp",EDGE,"E14.MirrorCS"),sQuery(id+"F0.wireOp",EDGE,"E15.MirrorCS"),sQuery(id+"F0.wireOp",EDGE,"E16.MirrorCS"),sQuery(id+"F0.wireOp",EDGE,"E17.MirrorCS"),sQuery(id+"F0.wireOp",EDGE,"E18.MirrorCS"),sQuery(id+"F0.wireOp",EDGE,"E19.MirrorCS"),sQuery(id+"F0.wireOp",EDGE,"E20.MirrorCS"),sQuery(id+"F0.wireOp",EDGE,"E21.MirrorCS"),sQuery(id+"F0.wireOp",EDGE,"E22.MirrorCS"),sQuery(id+"F0.wireOp",EDGE,"E23.MirrorCS"),sQuery(id+"F0.wireOp",EDGE,"E24.MirrorCS"),sQuery(id+"F0.wireOp",EDGE,"E25.MirrorCS"),sQuery(id+"F0.wireOp",EDGE,"E27.MirrorCS"),sQuery(id+"F0.wireOp",EDGE,"E28.MirrorCS"),sQuery(id+"F0.wireOp",EDGE,"E29.MirrorCS"),sQuery(id+"F0.wireOp",EDGE,"E30.MirrorCS"),sQuery(id+"F0.wireOp",EDGE,"E31.MirrorCS"),sQuery(id+"F0.wireOp",EDGE,"E32.MirrorCS"),sQuery(id+"F0.wireOp",EDGE,"E33.MirrorCS"),sQuery(id+"F0.wireOp",EDGE,"E34.MirrorCS"),sQuery(id+"F0.wireOp",EDGE,"E35.bottom"),sQuery(id+"F0.wireOp",EDGE,"E35.top"),sQuery(id+"F0.wireOp",EDGE,"E35.right"),sQuery(id+"F0.wireOp",EDGE,"E36"),sQuery(id+"F0.wireOp",EDGE,"E37"),sQuery(id+"F0.wireOp",EDGE,"E38.trimOffspring"),sQuery(id+"F0.wireOp",EDGE,"E39.0.1.0"),sQuery(id+"F0.wireOp",EDGE,"E39.0.1.1"),sQuery(id+"F0.wireOp",EDGE,"E39.0.1.2"),sQuery(id+"F0.wireOp",EDGE,"E39.0.1.3"),sQuery(id+"F0.wireOp",EDGE,"E39.0.1.4"),sQuery(id+"F0.wireOp",EDGE,"E39.0.2.0"),sQuery(id+"F0.wireOp",EDGE,"E39.0.2.1"),sQuery(id+"F0.wireOp",EDGE,"E39.0.2.2"),sQuery(id+"F0.wireOp",EDGE,"E39.0.2.3"),sQuery(id+"F0.wireOp",EDGE,"E39.0.2.4"),sQuery(id+"F0.wireOp",EDGE,"E39.0.3.0"),sQuery(id+"F0.wireOp",EDGE,"E39.0.3.1"),sQuery(id+"F0.wireOp",EDGE,"E39.0.3.2"),sQuery(id+"F0.wireOp",EDGE,"E39.0.3.3"),sQuery(id+"F0.wireOp",EDGE,"E39.0.3.4"),sQuery(id+"F0.wireOp",EDGE,"E40.trimOffspring"),sQuery(id+"F0.wireOp",EDGE,"E41.trimOffspring"),sQuery(id+"F0.wireOp",EDGE,"E42.trimOffspring"),sQuery(id+"F0.wireOp",EDGE,"E44.MirrorCS"),sQuery(id+"F0.wireOp",EDGE,"E45.MirrorCS"),sQuery(id+"F0.wireOp",EDGE,"E47.MirrorCS"),sQuery(id+"F0.wireOp",EDGE,"E48.MirrorCS"),sQuery(id+"F0.wireOp",EDGE,"E49.MirrorCS"),sQuery(id+"F0.wireOp",EDGE,"E50.MirrorCS"),sQuery(id+"F0.wireOp",EDGE,"E51.MirrorCS"),sQuery(id+"F0.wireOp",EDGE,"E52.MirrorCS"),sQuery(id+"F0.wireOp",EDGE,"E53.MirrorCS"),sQuery(id+"F0.wireOp",EDGE,"E54.MirrorCS"),sQuery(id+"F0.wireOp",EDGE,"E55.MirrorCS"),sQuery(id+"F0.wireOp",EDGE,"E56.MirrorCS"),sQuery(id+"F0.wireOp",EDGE,"E57.MirrorCS"),sQuery(id+"F0.wireOp",EDGE,"E58.MirrorCS"),sQuery(id+"F0.wireOp",EDGE,"E59.MirrorCS"),sQuery(id+"F0.wireOp",EDGE,"E60.MirrorCS"),sQuery(id+"F0.wireOp",EDGE,"E61.MirrorCS"),sQuery(id+"F0.wireOp",EDGE,"E62.MirrorCS"),sQuery(id+"F0.wireOp",EDGE,"E63.MirrorCS"),sQuery(id+"F0.wireOp",EDGE,"E64.MirrorCS"),sQuery(id+"F0.wireOp",EDGE,"E65.MirrorCS"),sQuery(id+"F0.wireOp",EDGE,"E66.MirrorCS"),sQuery(id+"F0.wireOp",EDGE,"E67.MirrorCS"),sQuery(id+"F0.wireOp",EDGE,"E68.MirrorCS"),sQuery(id+"F0.wireOp",EDGE,"E69.MirrorCS"),sQuery(id+"F0.wireOp",EDGE,"E70"),sQuery(id+"F0.wireOp",EDGE,"E71"),sQuery(id+"F0.wireOp",EDGE,"E72.trimOffspring")])],"isStart":false});
            var sketch = newSketch(context, id + "F6", { "sketchPlane" : qUnion([Q0])});
            skCircle(sketch, "E287", {"center": v(33, 65) * mm, "radius": 4 * mm});
            skCircle(sketch, "E288", {"center": v(57, 65) * mm, "radius": 4 * mm});
            skLineSegment(sketch, "E289", {"start": v(0, 65) * mm, "end": v(90, 65) * mm, "construction": true});
            skArc(sketch, "E290", {"start": v(33, 55) * mm, "mid": v(29, 51) * mm, "end": v(33, 47) * mm});
            skLineSegment(sketch, "E291", {"start": v(33, 55) * mm, "end": v(57, 55) * mm});
            skLineSegment(sketch, "E292", {"start": v(33, 47) * mm, "end": v(57, 47) * mm});
            skArc(sketch, "E293", {"start": v(57, 47) * mm, "mid": v(61, 51) * mm, "end": v(57, 55) * mm});
            skLineSegment(sketch, "E294", {"start": v(45, 90) * mm, "end": v(45, 0) * mm, "construction": true});
            skLineSegment(sketch, "E295", {"start": v(33, 51) * mm, "end": v(57, 51) * mm, "construction": true});
            skSolve(sketch);
        }
        {
            var Q0;
            Q0 = qSketchRegion(id + "F6", true);
            extrude(context, id + "F7", {"entities" : qUnion([Q0]), "operationType" : NewBodyOperationType.REMOVE, "endBound" : BoundingType.THROUGH_ALL, "oppositeDirection" : true, "depth" : 25 * mm});
        }
    });
